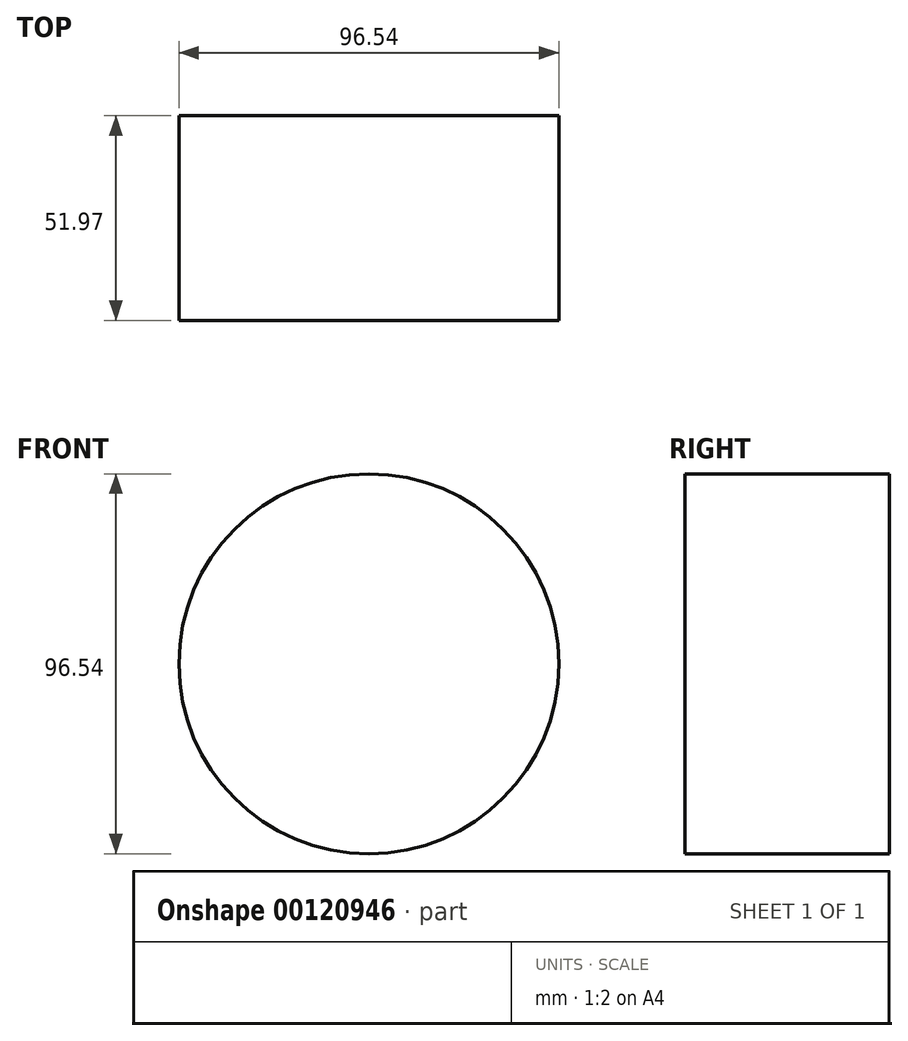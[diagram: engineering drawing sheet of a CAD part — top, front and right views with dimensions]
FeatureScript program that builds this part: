
annotation { "Feature Type Name" : "Feature", "Feature Type Description" : "" }
export const myFeature = defineFeature(function(context is Context, id is Id, definition is map)
    precondition{}
    {
        {
            var Q0;
            Q0=qCreatedBy(makeId("Front.planeOp"),FACE);
            var sketch = newSketch(context, id + "F0", { "sketchPlane" : qUnion([Q0])});
            skCircle(sketch, "E0", {"center": v(0, 0) * mm, "radius": 48.27 * mm});
            skSolve(sketch);
        }
        {
            var Q0;
            Q0=makeQuery(id+"F0.imprint","IMPRINT",FACE,{"disambiguationData":[TD([[makeQuery(id+"F0.imprint","IMPRINT",EDGE,{"derivedFrom":sQuery(id+"F0.wireOp",EDGE,"E0")}),1.0]])]});
            extrude(context, id + "F1", {"entities" : qUnion([Q0]), "depth" : 51.97 * mm});
        }
    });
